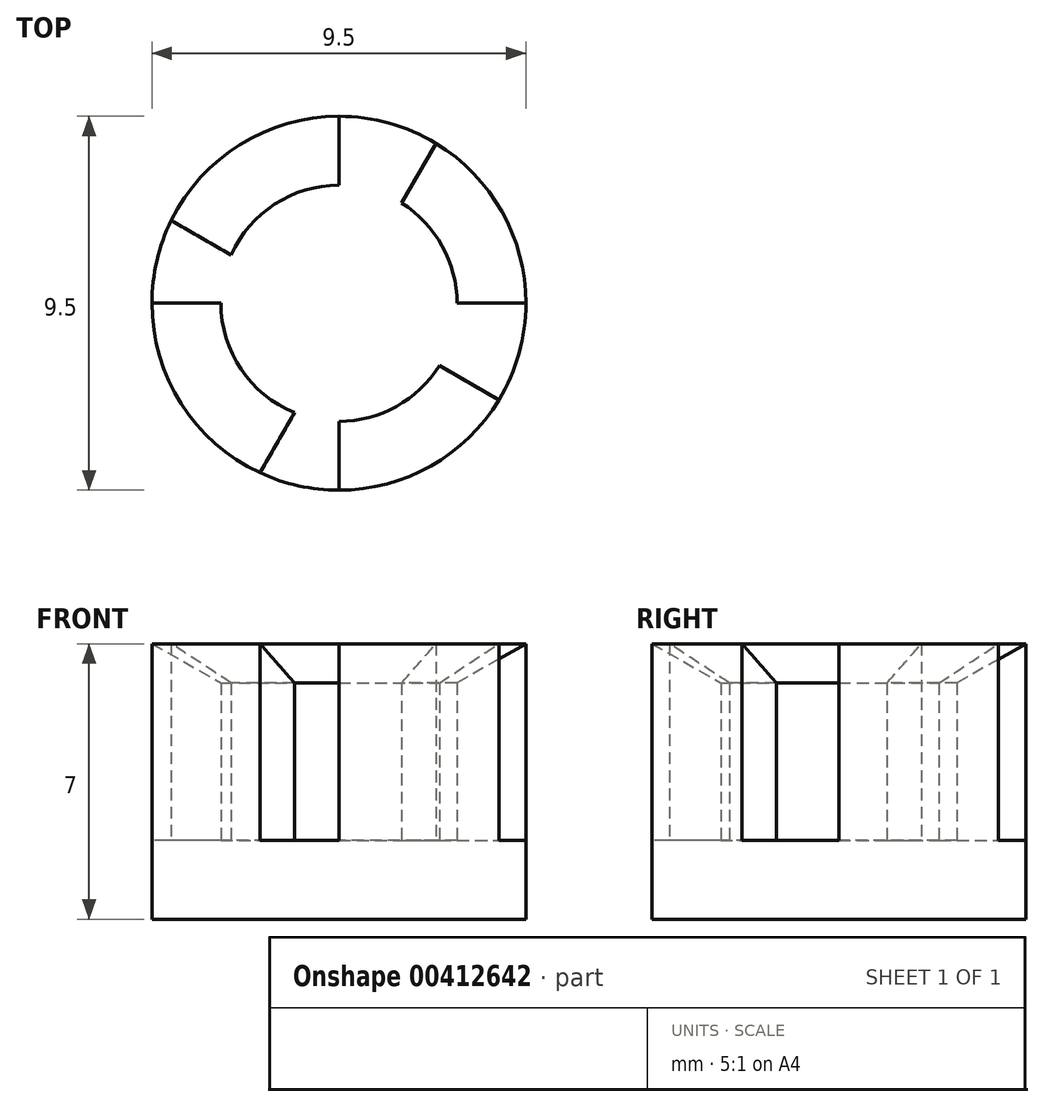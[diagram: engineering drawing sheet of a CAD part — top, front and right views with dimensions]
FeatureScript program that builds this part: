
annotation { "Feature Type Name" : "Feature", "Feature Type Description" : "" }
export const myFeature = defineFeature(function(context is Context, id is Id, definition is map)
    precondition{}
    {
        {
            var Q0;
            Q0=qCreatedBy(makeId("Top.planeOp"),FACE);
            var sketch = newSketch(context, id + "F0", { "sketchPlane" : qUnion([Q0])});
            skCircle(sketch, "E0", {"center": v(0, 0) * mm, "radius": 3 * mm});
            skCircle(sketch, "E1", {"center": v(0, 0) * mm, "radius": 4.75 * mm});
            skLineSegment(sketch, "E2", {"start": v(0, 3) * mm, "end": v(0, 4.75) * mm});
            skLineSegment(sketch, "E3", {"start": v(1.59, 2.54) * mm, "end": v(2.46, 4.06) * mm});
            skLineSegment(sketch, "E4", {"start": v(3, 0) * mm, "end": v(4.75, 0) * mm});
            skLineSegment(sketch, "E5", {"start": v(2.55, -1.58) * mm, "end": v(4.07, -2.46) * mm});
            skLineSegment(sketch, "E6", {"start": v(0, -3) * mm, "end": v(0, -4.75) * mm});
            skLineSegment(sketch, "E7", {"start": v(-3, 0) * mm, "end": v(-4.75, 0) * mm});
            skLineSegment(sketch, "E8", {"start": v(-2.74, 1.23) * mm, "end": v(-4.26, 2.1) * mm});
            skLineSegment(sketch, "E9", {"start": v(-1.13, -2.78) * mm, "end": v(-2, -4.3) * mm});
            skSolve(sketch);
        }
        {
            var Q0;
            {var subQ0=sQuery(id+"F0.wireOp",EDGE,"E0");var subQ4=makeQuery(id+"F0.imprint","INTERSECT",VERTEX,{"derivedFrom":[subQ0,sQuery(id+"F0.wireOp",EDGE,"E3")]});Q0=makeQuery(id+"F0.imprint","IMPRINT",FACE,{"disambiguationData":[TD([[makeQuery(id+"F0.imprint","IMPRINT",EDGE,{"disambiguationData":[TD([[subQ4,1.0]])],"derivedFrom":subQ0}),1.0]])]});}
            var Q1;
            {var subQ0=sQuery(id+"F0.wireOp",EDGE,"E6");Q1=makeQuery(id+"F0.imprint","IMPRINT",FACE,{"disambiguationData":[TD([[makeQuery(id+"F0.imprint","IMPRINT",EDGE,{"derivedFrom":subQ0}),-1.0]])]});}
            var Q2;
            {var subQ0=sQuery(id+"F0.wireOp",EDGE,"E4");Q2=makeQuery(id+"F0.imprint","IMPRINT",FACE,{"disambiguationData":[TD([[makeQuery(id+"F0.imprint","IMPRINT",EDGE,{"derivedFrom":subQ0}),-1.0]])]});}
            var Q3;
            {var subQ0=sQuery(id+"F0.wireOp",EDGE,"E7");Q3=makeQuery(id+"F0.imprint","IMPRINT",FACE,{"disambiguationData":[TD([[makeQuery(id+"F0.imprint","IMPRINT",EDGE,{"derivedFrom":subQ0}),-1.0]])]});}
            var Q4;
            {var subQ0=sQuery(id+"F0.wireOp",EDGE,"E2");Q4=makeQuery(id+"F0.imprint","IMPRINT",FACE,{"disambiguationData":[TD([[makeQuery(id+"F0.imprint","IMPRINT",EDGE,{"derivedFrom":subQ0}),-1.0]])]});}
            extrude(context, id + "F1", {"entities" : qUnion([Q0, Q1, Q2, Q3, Q4]), "depth" : 2 * mm});
        }
        {
            var Q0;
            {var subQ0=sQuery(id+"F0.wireOp",EDGE,"E7");Q0=makeQuery(id+"F0.imprint","IMPRINT",FACE,{"disambiguationData":[TD([[makeQuery(id+"F0.imprint","IMPRINT",EDGE,{"derivedFrom":subQ0}),1.0]])]});}
            var Q1;
            {var subQ0=sQuery(id+"F0.wireOp",EDGE,"E5");Q1=makeQuery(id+"F0.imprint","IMPRINT",FACE,{"disambiguationData":[TD([[makeQuery(id+"F0.imprint","IMPRINT",EDGE,{"derivedFrom":subQ0}),-1.0]])]});}
            var Q2;
            {var subQ0=sQuery(id+"F0.wireOp",EDGE,"E3");Q2=makeQuery(id+"F0.imprint","IMPRINT",FACE,{"disambiguationData":[TD([[makeQuery(id+"F0.imprint","IMPRINT",EDGE,{"derivedFrom":subQ0}),-1.0]])]});}
            var Q3;
            {var subQ0=sQuery(id+"F0.wireOp",EDGE,"E2");Q3=makeQuery(id+"F0.imprint","IMPRINT",FACE,{"disambiguationData":[TD([[makeQuery(id+"F0.imprint","IMPRINT",EDGE,{"derivedFrom":subQ0}),1.0]])]});}
            extrude(context, id + "F2", {"entities" : qUnion([Q0, Q1, Q2, Q3]), "operationType" : NewBodyOperationType.ADD, "depth" : 7 * mm});
        }
        {
            var Q0;
            {var subQ0=sQuery(id+"F0.wireOp",EDGE,"E0");Q0=makeQuery(id+"F2.opExtrude","CAP_EDGE",EDGE,{"disambiguationData":[OSD([subQ0]),TDD([makeQuery(id+"F0.imprint","IMPRINT",EDGE,{"disambiguationData":[TD([[makeQuery(id+"F0.imprint","INTERSECT",VERTEX,{"derivedFrom":[subQ0,sQuery(id+"F0.wireOp",EDGE,"E7")]}),-1.0]])],"derivedFrom":subQ0})])],"isStart":false});}
            var Q1;
            {var subQ0=sQuery(id+"F0.wireOp",EDGE,"E0");Q1=makeQuery(id+"F2.opExtrude","CAP_EDGE",EDGE,{"disambiguationData":[OSD([subQ0]),TDD([makeQuery(id+"F0.imprint","IMPRINT",EDGE,{"disambiguationData":[TD([[makeQuery(id+"F0.imprint","INTERSECT",VERTEX,{"derivedFrom":[subQ0,sQuery(id+"F0.wireOp",EDGE,"E2")]}),-1.0]])],"derivedFrom":subQ0})])],"isStart":false});}
            var Q2;
            {var subQ0=sQuery(id+"F0.wireOp",EDGE,"E0");Q2=makeQuery(id+"F2.opExtrude","CAP_EDGE",EDGE,{"disambiguationData":[OSD([subQ0]),TDD([makeQuery(id+"F0.imprint","IMPRINT",EDGE,{"disambiguationData":[TD([[makeQuery(id+"F0.imprint","INTERSECT",VERTEX,{"derivedFrom":[subQ0,sQuery(id+"F0.wireOp",EDGE,"E3")]}),1.0]])],"derivedFrom":subQ0})])],"isStart":false});}
            var Q3;
            {var subQ0=sQuery(id+"F0.wireOp",EDGE,"E0");Q3=makeQuery(id+"F2.opExtrude","CAP_EDGE",EDGE,{"disambiguationData":[OSD([subQ0]),TDD([makeQuery(id+"F0.imprint","IMPRINT",EDGE,{"disambiguationData":[TD([[makeQuery(id+"F0.imprint","INTERSECT",VERTEX,{"derivedFrom":[subQ0,sQuery(id+"F0.wireOp",EDGE,"E5")]}),1.0]])],"derivedFrom":subQ0})])],"isStart":false});}
            chamfer(context, id + "F3", {"entities" : qUnion([Q0, Q1, Q2, Q3]), "chamferType" : ChamferType.TWO_OFFSETS, "width1" : 1 * mm, "oppositeDirection" : false, "width2" : 1.75 * mm, "tangentPropagation" : true});
        }
    });
